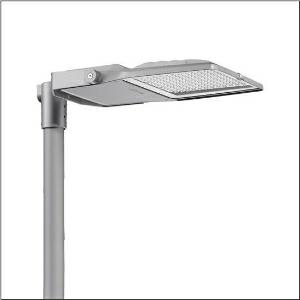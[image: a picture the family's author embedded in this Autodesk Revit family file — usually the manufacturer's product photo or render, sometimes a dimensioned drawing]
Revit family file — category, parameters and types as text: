
# Revit family: floodlight_fl_21_iq_midi___pl52_5xa7782f2d3a_028a
name_source: partatom
category: Lighting Fixtures
units: mm (PartAtom-declared; Revit-internal decimal feet)

## family parameters
Cut with Voids When Loaded = No
Host = Face
Light Source = No
Part Type = Normal
Room Calculation Point = No
Round Connector Dimension = Use Diameter
Shared = No

## types (1)
- --- (1 x LED, 35760 lm, 270.2 W, 3000K)
    Apparent Load = 270 VA
    CIE Flux Codes = 26 60 98 100 100
    Color Rendering = 70
    Color Temperature = 3000K
    Default Elevation = 1800 mm
    Description = Floodlight FL 21 iQ midi, floodlight, primary light control with lens, of PMMA, primary optical cover: protective disc, of toughened safety glass, transparent, light distribution: PL52, light emission: direct distribution, installation type: surface-mounted, LED, High Power LED, rated luminous flux: 35.760lm, luminous efficacy: 132lm/W, light colour: 730, colour temperature: 3000K, control gear: iQ Street-Remote/DALI, control: optimised constant luminous flux control (CLO 2.0), Desk-Remote (wireless, voltage-free reading and setting of iQ features in the workshop via application-optimized NFC function/RFID function), Smart-Wire, Night-Set, Temp-Guard, Auto-Match, Street-Remote, with terminal, 6-pole, mains connection: 220..240V, AC, 50/60Hz, start of lifetime: 270W, end of service life: 287W, reduction: 117W, luminaire housing, of diecast aluminium, powder-coated, Siteco® metallic grey (DB 702S), corrosivity category C5 mid according to DIN EN ISO 12944, suitable for swimming pools, chlorine-resistant, sealing non-destructively replaceable, please order mast flange separately, mast bracket, of steel, galvanised, powder-coated, Siteco® metallic grey (DB 702S), protection rating (complete): IP66, insulation class (complete): insulation class II (safety insulation), certification: CE, ENEC, VDE, protection symbol: D, impact resistance: IK08, permissible operating ambient temperature: -40..+40°C, permissible operating ambient temperature for outdoor applications: -40..+50°C, standard: DIN EN 12944, LABS conformity tested according to VDMA 24364:2018-05, packaging unit: 1 piece

Light Distribution: PL52
    Height = 76 mm
    Lamp = 1 x LED
    Lamp Light Flux = 35760 lm
    Lamp Power = 270.2 W
    Lamp count = 1
    Length = 657 mm
    Luminous efficacy = 132 lm/W
    Manufacturer = Siteco
    ModVariant = No
    Model = 5XA7782F2D3A
    Number of Poles = 1
    OnlyDefault = Yes
    Power Factor = 1
    Product Name = Floodlight FL 21 iQ midi | PL52
    Product group = floodlight | pylon annexe
    ProductGroupID = 6200
    Protection Class = Protection class II
    Protection Degree = IP 66
    RLX_Detail_Level = 1
    RLX_Emergency_Light_Flux = 0 lm
    RLX_Emergency_Type = 0
    RLX_Emergency_Type_DB = No
    RlxData = <blob elided: 154013 chars, md5=2608892f>
    Socket = socket
    Standby Power = 0 W
    System Light Flux = 35760 lm
    System Power = 270 W
    Type Comments = factory setting: luminous flux: 100 % | dim-lin: 254 | 620 mA
    Type Image = l_1007123.jpg
    URL = http://relux.com
    VarID = @adj_105636
    Voltage = 0 V
    Weight = 0.00 kg
    Width = 442 mm

## geometry (parser evidence)
native form markers: Blend x4, Sweep x14
no freeform markers — native parametric forms only
